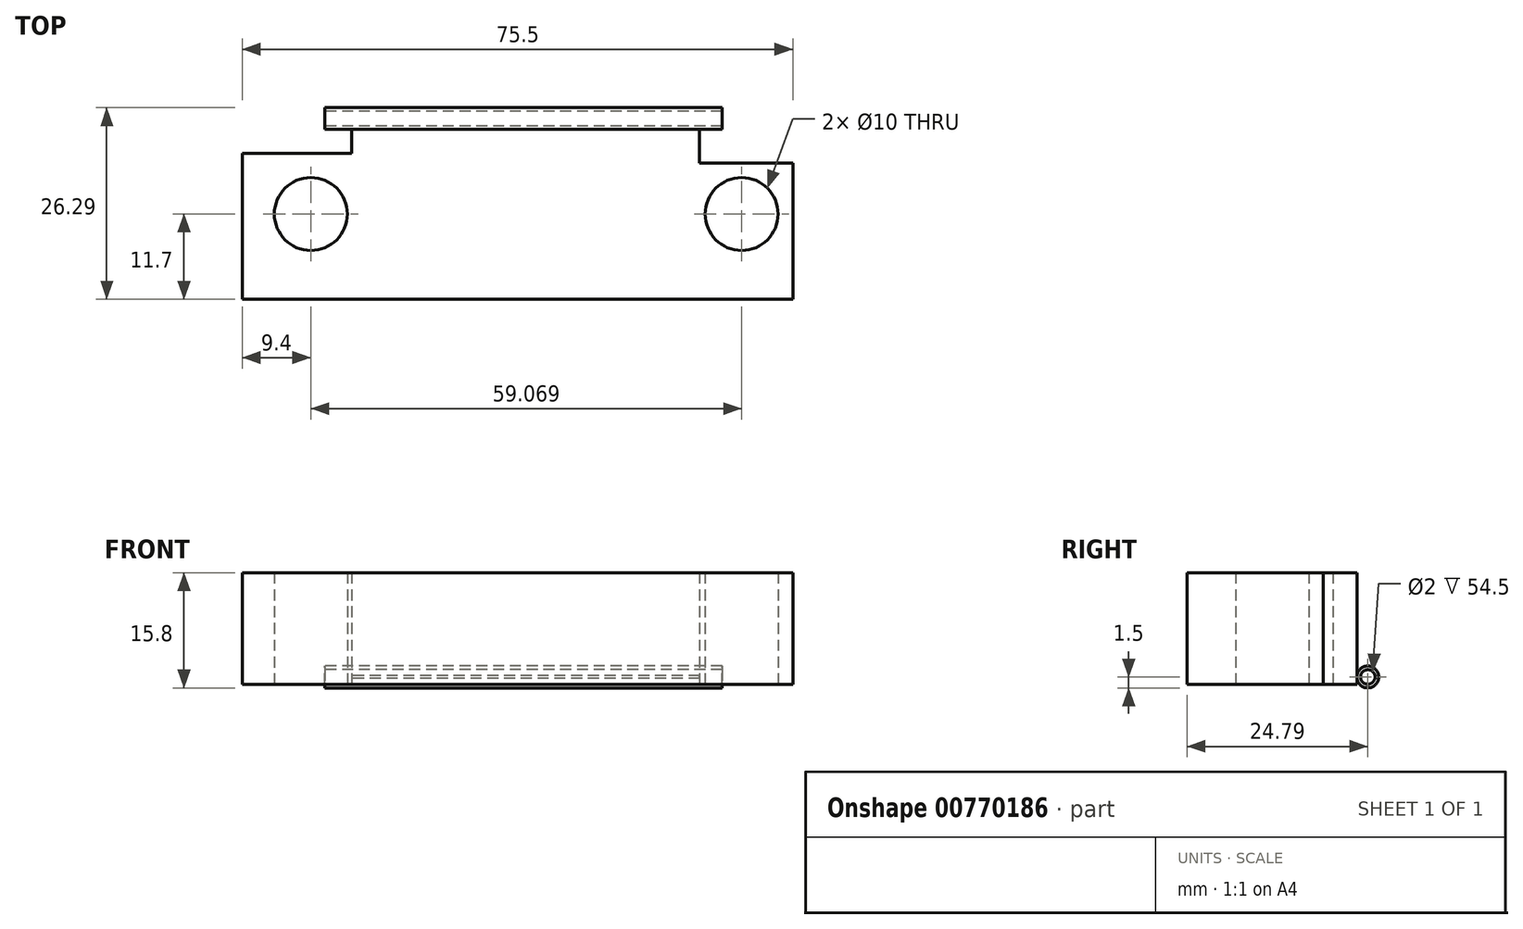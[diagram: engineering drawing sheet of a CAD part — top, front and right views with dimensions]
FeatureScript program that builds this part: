
annotation { "Feature Type Name" : "Feature", "Feature Type Description" : "" }
export const myFeature = defineFeature(function(context is Context, id is Id, definition is map)
    precondition{}
    {
        {
            var Q0;
            Q0=qCreatedBy(makeId("Top.planeOp"),FACE);
            var sketch = newSketch(context, id + "F0", { "sketchPlane" : qUnion([Q0])});
            skLineSegment(sketch, "E0", {"start": v(0, 20) * mm, "end": v(0, 0) * mm});
            skLineSegment(sketch, "E1", {"start": v(0, 0) * mm, "end": v(75.5, 0) * mm});
            skLineSegment(sketch, "E2", {"start": v(75.5, 0) * mm, "end": v(75.5, 18.7) * mm});
            skLineSegment(sketch, "E3", {"start": v(75.5, 18.7) * mm, "end": v(62.7, 18.7) * mm});
            skLineSegment(sketch, "E4", {"start": v(62.7, 18.7) * mm, "end": v(62.7, 23.3) * mm});
            skLineSegment(sketch, "E5", {"start": v(62.7, 23.3) * mm, "end": v(15, 23.3) * mm});
            skLineSegment(sketch, "E6", {"start": v(15, 23.3) * mm, "end": v(15, 20) * mm});
            skLineSegment(sketch, "E7", {"start": v(15, 20) * mm, "end": v(0, 20) * mm});
            skCircle(sketch, "E8", {"center": v(9.4, 11.7) * mm, "radius": 5 * mm});
            skCircle(sketch, "E9", {"center": v(68.47, 11.7) * mm, "radius": 5 * mm});
            skCircle(sketch, "E10", {"center": v(38.93, 91.94) * mm, "radius": 85.5 * mm, "construction": true});
            skLineSegment(sketch, "E11", {"start": v(38.93, 91.94) * mm, "end": v(38.93, 6.44) * mm, "construction": true});
            skCircle(sketch, "E12", {"center": v(38.93, 6.44) * mm, "radius": 30 * mm, "construction": true});
            skSolve(sketch);
        }
        {
            var Q0;
            Q0=makeQuery(id+"F0.imprint","IMPRINT",FACE,{"disambiguationData":[TD([[makeQuery(id+"F0.imprint","IMPRINT",EDGE,{"derivedFrom":sQuery(id+"F0.wireOp",EDGE,"E0")}),1.0]])]});
            extrude(context, id + "F1", {"entities" : qUnion([Q0]), "depth" : 15.3 * mm, "offsetDistance" : 25 * mm});
        }
        {
            var Q0;
            Q0=makeQuery(id+"F1.opExtrude","SWEPT_FACE",FACE,{"disambiguationData":[OSD([sQuery(id+"F0.wireOp",EDGE,"E6")])]});
            cPlane(context, id + "F2", {"entities" : qUnion([Q0]), "cplaneType" : CPlaneType.OFFSET, "offset" : 0 * mm, "width" : 150 * mm, "height" : 150 * mm});
        }
        {
            var Q0;
            Q0=qCreatedBy(id+"F2.planeOp",FACE);
            var sketch = newSketch(context, id + "F3", { "sketchPlane" : qUnion([Q0])});
            skCircle(sketch, "E13", {"center": v(-24.79, 1) * mm, "radius": 1.5 * mm});
            skCircle(sketch, "E14", {"center": v(-24.79, 1) * mm, "radius": 1 * mm});
            skSolve(sketch);
        }
        {
            var Q0;
            Q0=makeQuery(id+"F3.imprint","IMPRINT",FACE,{"disambiguationData":[TD([[makeQuery(id+"F3.imprint","IMPRINT",EDGE,{"derivedFrom":sQuery(id+"F3.wireOp",EDGE,"E13")}),1.0]])]});
            extrude(context, id + "F4", {"entities" : qUnion([Q0]), "operationType" : NewBodyOperationType.ADD, "oppositeDirection" : true, "depth" : (54.5 - 3.7) * mm, "offsetDistance" : 25 * mm, "hasSecondDirection" : true, "secondDirectionOppositeDirection" : false, "secondDirectionDepth" : 3.7 * mm});
        }
    });
